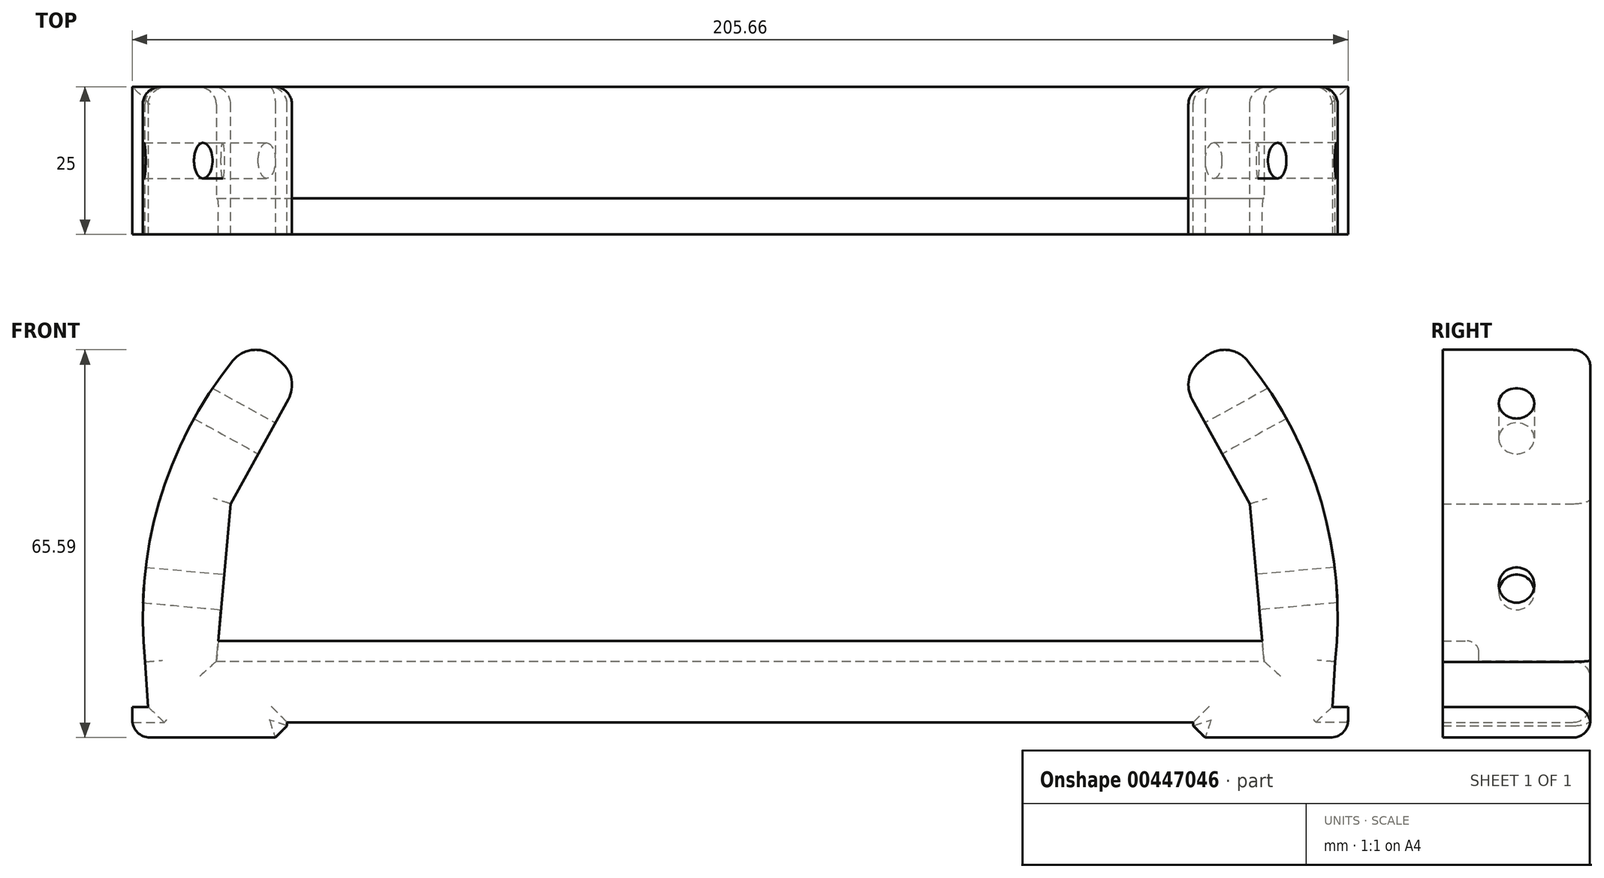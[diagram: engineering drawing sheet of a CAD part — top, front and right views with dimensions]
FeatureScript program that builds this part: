
annotation { "Feature Type Name" : "Feature", "Feature Type Description" : "" }
export const myFeature = defineFeature(function(context is Context, id is Id, definition is map)
    precondition{}
    {
        {
            var Q0;
            Q0=qCreatedBy(makeId("Front.planeOp"),FACE);
            var sketch = newSketch(context, id + "F0", { "sketchPlane" : qUnion([Q0])});
            skLineSegment(sketch, "E0.bottom", {"start": v(0, 0) * mm, "end": v(-99.24, 0) * mm});
            skLineSegment(sketch, "E0.top", {"start": v(0, 10.34) * mm, "end": v(-99.24, 10.34) * mm});
            skLineSegment(sketch, "E0.left", {"start": v(0, 0) * mm, "end": v(0, 10.34) * mm});
            skLineSegment(sketch, "E0.right", {"start": v(-99.24, 0) * mm, "end": v(-99.24, 10.34) * mm});
            skLineSegment(sketch, "E1.bottom", {"start": v(-99.24, 0) * mm, "end": v(-102.83, 0) * mm});
            skLineSegment(sketch, "E1.top", {"start": v(-99.24, 2.6) * mm, "end": v(-102.83, 2.6) * mm});
            skLineSegment(sketch, "E1.left", {"start": v(-99.24, 0) * mm, "end": v(-99.24, 2.6) * mm});
            skLineSegment(sketch, "E1.right", {"start": v(-102.83, 0) * mm, "end": v(-102.83, 2.6) * mm});
            skLineSegment(sketch, "E2.bottom", {"start": v(-102.83, 0) * mm, "end": v(-76.64, 0) * mm});
            skLineSegment(sketch, "E2.top", {"start": v(-102.83, -2.6) * mm, "end": v(-76.64, -2.6) * mm});
            skLineSegment(sketch, "E2.left", {"start": v(-102.83, 0) * mm, "end": v(-102.83, -2.6) * mm});
            skLineSegment(sketch, "E2.right", {"start": v(-76.64, 0) * mm, "end": v(-76.64, -2.6) * mm});
            skSolve(sketch);
        }
        {
            var Q0;
            Q0=qCreatedBy(makeId("Front.planeOp"),FACE);
            var sketch = newSketch(context, id + "F1", { "sketchPlane" : qUnion([Q0])});
            skPoint(sketch, "E3", {"position": v(-100, 0) * mm});
            skPoint(sketch, "E4", {"position": v(-82.5, 65) * mm});
            skArc(sketch, "E5", {"start": v(-82.5, 65) * mm, "mid": v(-97.56, 39.6) * mm, "end": v(-100.65, 10.23) * mm});
            skLineSegment(sketch, "E6", {"start": v(-100.65, 10.23) * mm, "end": v(-100, 0) * mm});
            skLineSegment(sketch, "E7", {"start": v(-82.5, 65) * mm, "end": v(-74.46, 58.23) * mm});
            skLineSegment(sketch, "E8", {"start": v(-100, 0) * mm, "end": v(-88.64, 0) * mm});
            skLineSegment(sketch, "E9", {"start": v(-74.46, 58.23) * mm, "end": v(-86.19, 36.96) * mm});
            skLineSegment(sketch, "E10", {"start": v(-86.19, 36.96) * mm, "end": v(-88.64, 9.96) * mm});
            skLineSegment(sketch, "E11", {"start": v(-88.64, 9.96) * mm, "end": v(-88.64, 0) * mm});
            skSolve(sketch);
        }
        {
            var Q0;
            {var subQ0=sQuery(id+"F0.wireOp",EDGE,"E0.bottom");Q0=makeQuery(id+"F0.imprint","IMPRINT",FACE,{"disambiguationData":[TD([[makeQuery(id+"F0.imprint","IMPRINT",EDGE,{"derivedFrom":subQ0}),-1.0]])]});}
            var Q1;
            Q1=makeQuery(id+"F0.imprint","IMPRINT",FACE,{"disambiguationData":[TD([[makeQuery(id+"F0.imprint","IMPRINT",EDGE,{"derivedFrom":sQuery(id+"F0.wireOp",EDGE,"E2.top")}),1.0]])]});
            var Q2;
            Q2=makeQuery(id+"F0.imprint","IMPRINT",FACE,{"disambiguationData":[TD([[makeQuery(id+"F0.imprint","IMPRINT",EDGE,{"derivedFrom":sQuery(id+"F0.wireOp",EDGE,"E1.top")}),1.0]])]});
            extrude(context, id + "F2", {"entities" : qUnion([Q0, Q1, Q2]), "endBound" : BoundingType.SYMMETRIC, "depth" : 25 * mm});
        }
        {
            var Q0;
            Q0=makeQuery(id+"F1.imprint","IMPRINT",FACE,{"disambiguationData":[TD([[makeQuery(id+"F1.imprint","IMPRINT",EDGE,{"derivedFrom":sQuery(id+"F1.wireOp",EDGE,"E5")}),1.0]])]});
            extrude(context, id + "F3", {"entities" : qUnion([Q0]), "operationType" : NewBodyOperationType.ADD, "endBound" : BoundingType.SYMMETRIC, "depth" : 25 * mm});
        }
        {
            var Q0;
            Q0=makeQuery(id+"F2.opExtrude","SWEPT_FACE",FACE,{"disambiguationData":[OSD([sQuery(id+"F0.wireOp",EDGE,"E0.left")])]});
            var sketch = newSketch(context, id + "F4", { "sketchPlane" : qUnion([Q0])});
            skLineSegment(sketch, "E12.bottom", {"start": v(-12.5, 10.34) * mm, "end": v(-6.36, 10.34) * mm});
            skLineSegment(sketch, "E12.top", {"start": v(-12.5, 13.75) * mm, "end": v(-6.36, 13.75) * mm});
            skLineSegment(sketch, "E12.left", {"start": v(-12.5, 10.34) * mm, "end": v(-12.5, 13.75) * mm});
            skLineSegment(sketch, "E12.right", {"start": v(-6.36, 10.34) * mm, "end": v(-6.36, 13.75) * mm});
            skSolve(sketch);
        }
        {
            var Q0;
            Q0=makeQuery(id+"F3.opExtrude","SWEPT_FACE",FACE,{"disambiguationData":[OSD([sQuery(id+"F1.wireOp",EDGE,"E10")])]});
            var sketch = newSketch(context, id + "F5", { "sketchPlane" : qUnion([Q0])});
            skPoint(sketch, "E13", {"position": v(0, 14) * mm});
            skSolve(sketch);
        }
        {
            var Q0;
            Q0 = qSketchRegion(id + "F4", true);
            extrude(context, id + "F6", {"entities" : qUnion([Q0]), "operationType" : NewBodyOperationType.ADD, "depth" : -100 * mm});
        }
        {
            var Q0;
            Q0=sQuery(id+"F5.wireOp",VERTEX,"E13");
            var Q1;
            Q1=makeQuery(id+"F2.opExtrude","SWEPT_BODY",BODY,{"disambiguationData":[OSD([sQuery(id+"F0.wireOp",EDGE,"E0.bottom"),sQuery(id+"F0.wireOp",EDGE,"E0.top"),sQuery(id+"F0.wireOp",EDGE,"E0.left"),sQuery(id+"F0.wireOp",EDGE,"E0.right"),sQuery(id+"F0.wireOp",EDGE,"E1.top"),sQuery(id+"F0.wireOp",EDGE,"E1.right"),sQuery(id+"F0.wireOp",EDGE,"E2.top"),sQuery(id+"F0.wireOp",EDGE,"E2.left"),sQuery(id+"F0.wireOp",EDGE,"E2.right")])]});
            hole(context, id + "F7", {"style" : HoleStyle.SIMPLE, "endStyle" : HoleEndStyle.THROUGH, "holeDiameter" : 6 * mm, "isTappedThrough" : true, "tappedDepth" : 12 * mm, "tapClearance" : 3, "locations" : qUnion([Q0]), "scope" : qUnion([Q1])});
        }
        {
            var Q0;
            Q0=makeQuery(id+"F3.opExtrude","SWEPT_FACE",FACE,{"disambiguationData":[OSD([sQuery(id+"F1.wireOp",EDGE,"E9")])]});
            var sketch = newSketch(context, id + "F8", { "sketchPlane" : qUnion([Q0])});
            skPoint(sketch, "E14", {"position": v(0, 3.38) * mm});
            skSolve(sketch);
        }
        {
            var Q0;
            Q0=sQuery(id+"F8.wireOp",VERTEX,"E14");
            var Q1;
            Q1=makeQuery(id+"F2.opExtrude","SWEPT_BODY",BODY,{"disambiguationData":[OSD([sQuery(id+"F0.wireOp",EDGE,"E0.bottom"),sQuery(id+"F0.wireOp",EDGE,"E0.top"),sQuery(id+"F0.wireOp",EDGE,"E0.left"),sQuery(id+"F0.wireOp",EDGE,"E0.right"),sQuery(id+"F0.wireOp",EDGE,"E1.top"),sQuery(id+"F0.wireOp",EDGE,"E1.right"),sQuery(id+"F0.wireOp",EDGE,"E2.top"),sQuery(id+"F0.wireOp",EDGE,"E2.left"),sQuery(id+"F0.wireOp",EDGE,"E2.right")])]});
            hole(context, id + "F9", {"style" : HoleStyle.SIMPLE, "endStyle" : HoleEndStyle.THROUGH, "holeDiameter" : 6 * mm, "isTappedThrough" : true, "tappedDepth" : 12 * mm, "tapClearance" : 3, "locations" : qUnion([Q0]), "scope" : qUnion([Q1])});
        }
        {
            var Q0;
            Q0=makeQuery(id+"F2.opExtrude","CAP_EDGE",EDGE,{"disambiguationData":[OSD([sQuery(id+"F0.wireOp",EDGE,"E0.top")])],"isStart":true});
            var Q1;
            Q1=makeQuery(id+"F2.opExtrude","CAP_EDGE",EDGE,{"disambiguationData":[OSD([sQuery(id+"F0.wireOp",EDGE,"E0.bottom")])],"isStart":true});
            var Q2;
            Q2=makeQuery(id+"F2.opExtrude","CAP_EDGE",EDGE,{"disambiguationData":[OSD([sQuery(id+"F0.wireOp",EDGE,"E2.right")])],"isStart":true});
            var Q3;
            Q3=makeQuery(id+"F2.opExtrude","CAP_EDGE",EDGE,{"disambiguationData":[OSD([sQuery(id+"F0.wireOp",EDGE,"E2.top")])],"isStart":true});
            var Q4;
            Q4=makeQuery(id+"F3.opExtrude","CAP_EDGE",EDGE,{"disambiguationData":[OSD([sQuery(id+"F1.wireOp",EDGE,"E5")])],"isStart":true});
            var Q5;
            Q5=makeQuery(id+"F3.opExtrude","CAP_EDGE",EDGE,{"disambiguationData":[OSD([sQuery(id+"F1.wireOp",EDGE,"E7")])],"isStart":true});
            var Q6;
            Q6=makeQuery(id+"F3.opExtrude","CAP_EDGE",EDGE,{"disambiguationData":[OSD([sQuery(id+"F1.wireOp",EDGE,"E9")])],"isStart":true});
            var Q7;
            Q7=makeQuery(id+"F3.opExtrude","CAP_EDGE",EDGE,{"disambiguationData":[OSD([sQuery(id+"F1.wireOp",EDGE,"E10")])],"isStart":true});
            var Q8;
            Q8=makeQuery(id+"F3.opExtrude","CAP_EDGE",EDGE,{"disambiguationData":[OSD([sQuery(id+"F1.wireOp",EDGE,"E6")])],"isStart":true});
            var Q9;
            Q9=makeQuery(id+"F2.opExtrude","CAP_EDGE",EDGE,{"disambiguationData":[OSD([sQuery(id+"F0.wireOp",EDGE,"E1.top")])],"isStart":true});
            fillet(context, id + "F10", {"entities" : qUnion([Q0, Q1, Q2, Q3, Q4, Q5, Q6, Q7, Q8, Q9]), "radius" : 3 * mm, "tangentPropagation" : true, "allowEdgeOverflow" : false});
        }
        {
            var Q0;
            Q0=makeQuery(id+"F2.opExtrude","SWEPT_EDGE",EDGE,{"disambiguationData":[OSD([sQuery(id+"F0.wireOp",EDGE,"E2.top"),sQuery(id+"F0.wireOp",EDGE,"E2.left")])]});
            fillet(context, id + "F11", {"entities" : qUnion([Q0]), "radius" : 3 * mm, "tangentPropagation" : true, "allowEdgeOverflow" : false});
        }
        {
            var Q0;
            Q0=makeQuery(id+"F2.opExtrude","SWEPT_EDGE",EDGE,{"disambiguationData":[OSD([sQuery(id+"F0.wireOp",EDGE,"E2.top"),sQuery(id+"F0.wireOp",EDGE,"E2.right")])]});
            chamfer(context, id + "F12", {"entities" : qUnion([Q0]), "width" : 2 * mm, "tangentPropagation" : true});
        }
        {
            var Q0;
            Q0=makeQuery(id+"F3.opExtrude","SWEPT_EDGE",EDGE,{"disambiguationData":[OSD([sQuery(id+"F1.wireOp",EDGE,"E7"),sQuery(id+"F1.wireOp",EDGE,"E9")])]});
            var Q1;
            Q1=makeQuery(id+"F3.opExtrude","SWEPT_EDGE",EDGE,{"disambiguationData":[OSD([sQuery(id+"F1.wireOp",EDGE,"E5"),sQuery(id+"F1.wireOp",EDGE,"E7")])]});
            fillet(context, id + "F13", {"entities" : qUnion([Q0, Q1]), "radius" : 5 * mm, "tangentPropagation" : true, "allowEdgeOverflow" : false});
        }
        {
            var Q0;
            Q0=makeQuery(id+"F6.opExtrude","SWEPT_EDGE",EDGE,{"disambiguationData":[OSD([sQuery(id+"F4.wireOp",EDGE,"E12.top"),sQuery(id+"F4.wireOp",EDGE,"E12.right")])]});
            fillet(context, id + "F14", {"entities" : qUnion([Q0]), "radius" : 2 * mm, "tangentPropagation" : true, "allowEdgeOverflow" : false});
        }
        {
            var Q0;
            Q0=makeQuery(id+"F2.opExtrude","SWEPT_BODY",BODY,{"disambiguationData":[OSD([sQuery(id+"F0.wireOp",EDGE,"E0.bottom"),sQuery(id+"F0.wireOp",EDGE,"E0.top"),sQuery(id+"F0.wireOp",EDGE,"E0.left"),sQuery(id+"F0.wireOp",EDGE,"E0.right"),sQuery(id+"F0.wireOp",EDGE,"E1.top"),sQuery(id+"F0.wireOp",EDGE,"E1.right"),sQuery(id+"F0.wireOp",EDGE,"E2.top"),sQuery(id+"F0.wireOp",EDGE,"E2.left"),sQuery(id+"F0.wireOp",EDGE,"E2.right")])]});
            var Q1;
            Q1=makeQuery(id+"F6.boolean.opBoolean","MERGE",FACE,{"derivedFrom":[makeQuery(id+"F2.opExtrude","SWEPT_FACE",FACE,{"disambiguationData":[OSD([sQuery(id+"F0.wireOp",EDGE,"E0.left")])]}),makeQuery(id+"F6.opExtrude","CAP_FACE",FACE,{"disambiguationData":[OSD([sQuery(id+"F4.wireOp",EDGE,"E12.bottom"),sQuery(id+"F4.wireOp",EDGE,"E12.top"),sQuery(id+"F4.wireOp",EDGE,"E12.left"),sQuery(id+"F4.wireOp",EDGE,"E12.right")])],"isStart":true})]});
            mirror(context, id + "F15", {"operationType" : NewBodyOperationType.ADD, "entities" : qUnion([Q0]), "mirrorPlane" : qUnion([Q1])});
        }
    });
